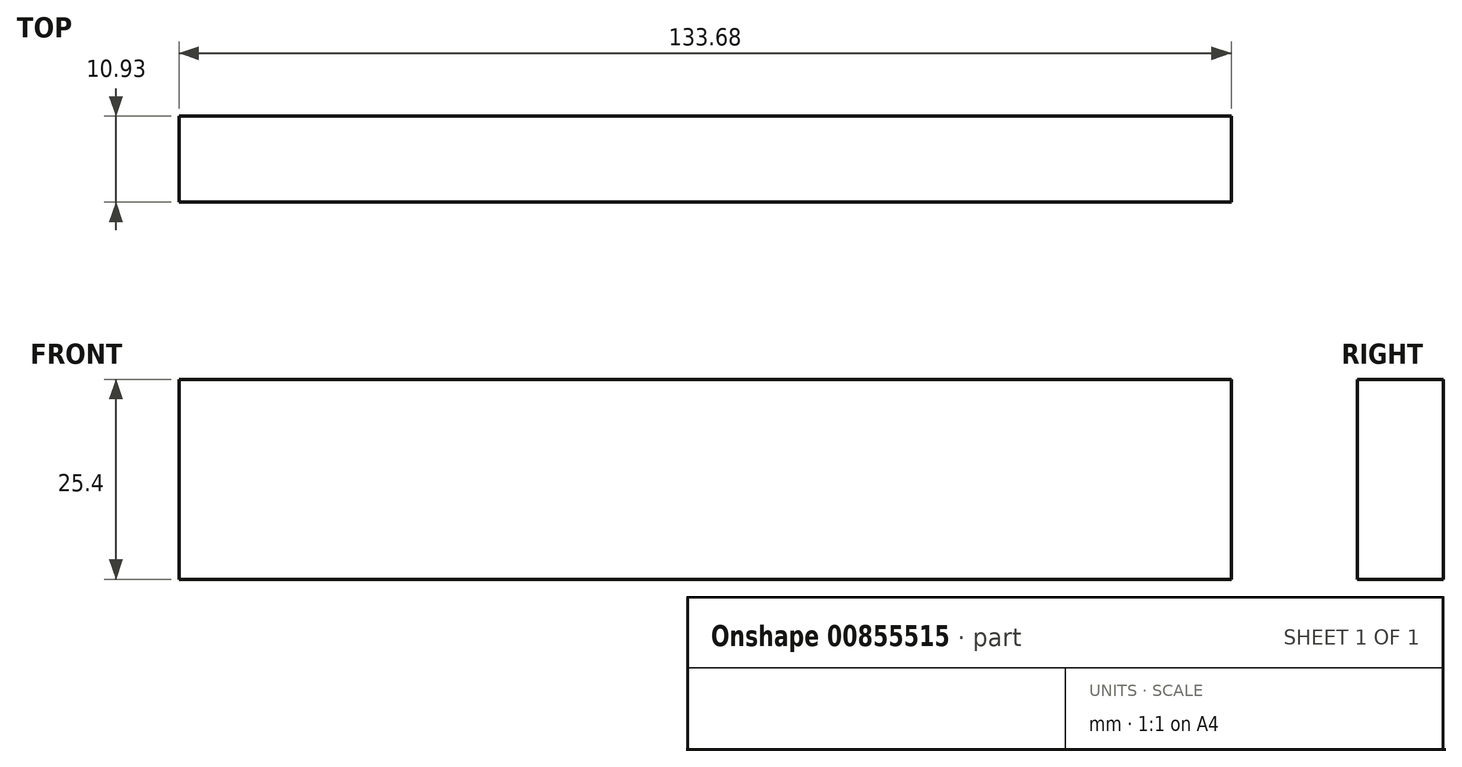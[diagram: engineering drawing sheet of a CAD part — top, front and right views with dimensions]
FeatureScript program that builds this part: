
annotation { "Feature Type Name" : "Feature", "Feature Type Description" : "" }
export const myFeature = defineFeature(function(context is Context, id is Id, definition is map)
    precondition{}
    {
        {
            var Q0;
            Q0=qCreatedBy(makeId("Top.planeOp"),FACE);
            var sketch = newSketch(context, id + "F0", { "sketchPlane" : qUnion([Q0])});
            skLineSegment(sketch, "E0.bottom", {"start": v(-72.59, 8.32) * mm, "end": v(72.59, 8.32) * mm});
            skLineSegment(sketch, "E0.top", {"start": v(-72.59, -8.32) * mm, "end": v(72.59, -8.32) * mm});
            skLineSegment(sketch, "E0.left", {"start": v(-72.59, 8.32) * mm, "end": v(-72.59, -8.32) * mm});
            skLineSegment(sketch, "E0.right", {"start": v(72.59, 8.32) * mm, "end": v(72.59, -8.32) * mm});
            skPoint(sketch, "E0.middle", {"position": v(0, 0) * mm});
            skLineSegment(sketch, "E1.bottom", {"start": v(-66.84, 19.25) * mm, "end": v(66.84, 19.25) * mm});
            skLineSegment(sketch, "E1.top", {"start": v(-66.84, 7.75) * mm, "end": v(66.84, 7.75) * mm});
            skLineSegment(sketch, "E1.left", {"start": v(-66.84, 19.25) * mm, "end": v(-66.84, 7.75) * mm});
            skLineSegment(sketch, "E1.right", {"start": v(66.84, 19.25) * mm, "end": v(66.84, 7.75) * mm});
            skPoint(sketch, "E1.middle", {"position": v(0, 13.5) * mm});
            skSolve(sketch);
        }
        {
            var Q0;
            {var subQ5=sQuery(id+"F0.wireOp",EDGE,"E1.bottom");Q0=makeQuery(id+"F0.imprint","IMPRINT",FACE,{"disambiguationData":[TD([[makeQuery(id+"F0.imprint","IMPRINT",EDGE,{"derivedFrom":subQ5}),-1.0]])]});}
            extrude(context, id + "F1", {"entities" : qUnion([Q0]), "depth" : 25.4 * mm, "offsetDistance" : 25.4 * mm});
        }
    });
